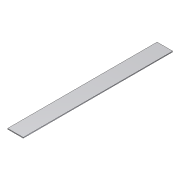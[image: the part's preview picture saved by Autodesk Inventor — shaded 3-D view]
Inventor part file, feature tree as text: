
AUTODESK INVENTOR PART (.ipt)
format: ipt  version: unknown  size: 160,256 bytes
history: native  units: in
note: dims shown in document units (in); Inventor stores cm internally (conversion verified against a paired STEP export)
features: extrude x1, sketch x1
ambient origin geometry x8: Origin, YZ Plane, XZ Plane, XY Plane, X Axis, Y Axis, Z Axis, Center Point
bodies: Solid1 (feature_tree)
feature tree (2):
  extrude  "Extrusion1"  Depth=5.0in
  sketch  "Sketch1"  dims[d0=0.25in d1=5.0in d2=48.0in d3=0.0in]
